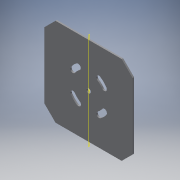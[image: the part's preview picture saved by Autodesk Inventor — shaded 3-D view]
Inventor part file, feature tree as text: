
AUTODESK INVENTOR PART (.ipt)
format: ipt  version: 2017 (Build 210142000, 142)  size: 142,336 bytes
history: native  units: mm
features: extrude x1, other x1, chamfer x1, plane x1, sketch x1
ambient origin geometry x8: Origin, YZ Plane, XZ Plane, XY Plane, X Axis, Y Axis, Z Axis, Center Point
bodies: Solid1 (feature_tree)
feature tree (5):
  extrude  "Extrusion1"  Depth=304.8mm
  other  "Work Axis1"
  chamfer  "Chamfer1"  Distance=5.0mm
  plane  "Work Plane1"
  sketch  "Sketch1"  dims[d1=304.8mm d2=304.8mm d3=5.0mm d4=0.0mm d5=35.0mm d6=38.1mm d7=2.0mm d8=45.0deg d9=40.0mm d11=360.0deg d13=18.0mm d14=15.0mm]
